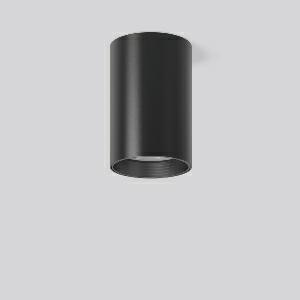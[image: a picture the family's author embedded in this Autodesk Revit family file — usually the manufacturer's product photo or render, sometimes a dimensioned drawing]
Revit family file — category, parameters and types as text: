
# Revit family: heledon_maxi_a_931243_003_76_7f32
name_source: partatom
category: Lighting Fixtures
units: mm (PartAtom-declared; Revit-internal decimal feet)

## family parameters
Cut with Voids When Loaded = No
Host = Face
Light Source = No
Part Type = Normal
Room Calculation Point = No
Round Connector Dimension = Use Diameter
Shared = No

## types (1)
- HELEDON maxi A (1 x LED Modul 920 meat+, 1900 lm, 2000)
    Apparent Load = 33 VA
    Approval mark = CE
    CIE Flux Codes = 96 99 100 100 100
    Color Rendering = 90
    Color Temperature = 2000
    Default Elevation = 1800 mm
    Description = Series: HELEDON maxi
Cylindrical surface-mounted downlight. Housing: die-cast aluminium, powder-coated. Internal ceiling frame polycarbonate with bayonet mounting. Black plastic ring and recessed LED to prevent glare from the side. Optical assembly with lens made of plastic (polycarbonate) for the best homogeneous light distribution - can be changed without tools. Special LED for illumination of meat included. Suitable for Ceiling mounting. Easy installation with a separate ceiling frame with bayonet mounting and plug connection. Driver integrated. Connected via plug-in connector. High quality converter without flickering and stroboscopic effect. The following accessories can be mounted without use of tools: interchangeable lenses, decorative glasses, honeycomb louvre, clear and frosted diffusers, white interchangeable plastic ring. 
Colour: deep black, matt (RAL 9005)
Diameter: 123 mm
Height: 183 mm
Lamp: LED
Socket: without socket
Colour temperature: meat +
System power: 33 W
Rated luminous flux: 1900 lm
Luminous efficiency: 58 lm/W
Control gear: Converter, dimmable, DALI
Protection class: I
Type of protection: IP 20
    Height = 183 mm
    Lamp = 1 x LED Modul 920 meat+
    Lamp Light Flux = 1900 lm
    Lamp count = 1
    Length = 123 mm
    Lifetime = 50000 h
    Luminous efficacy = 58 lm/W
    Manufacturer = RZB
    ModVariant = No
    Model = 931243.003.76
    Mounting Place = Ceiling
    Mounting Type = Surface mounted
    Number of Poles = 1
    OnlyDefault = Yes
    Power Factor = 1
    Product Name = HELEDON maxi A
    Product group = Surface mounted downlights
    ProductGroupID = 302
    Protection Class = Protection class I
    Protection Degree = IP 20
    RLX_Detail_Level = 1
    RLX_Emergency_Light_Flux = 0 lm
    RLX_Emergency_Type = 0
    RLX_Emergency_Type_DB = No
    RlxData = <blob elided: 96841 chars, md5=fe074a1a>
    Socket = socket
    Standby Power = 0 W
    System Light Flux = 1900 lm
    System Power = 33 W
    Type Comments = Product without accessories
    Type Image = 931193.003.jpg
    URL = http://relux.com
    VarID = ---
    Voltage = 230 V
    Voltage Range = 220-240 V
    Weight = 0.00 kg
    Width = 0 mm  [stored 0 ft]

note: [stored X ft] marks values corroborated as IEEE doubles in the binary element streams (Revit-internal decimal feet)

## geometry (parser evidence)
native form markers: Blend x4, Sweep x9
no freeform markers — native parametric forms only
